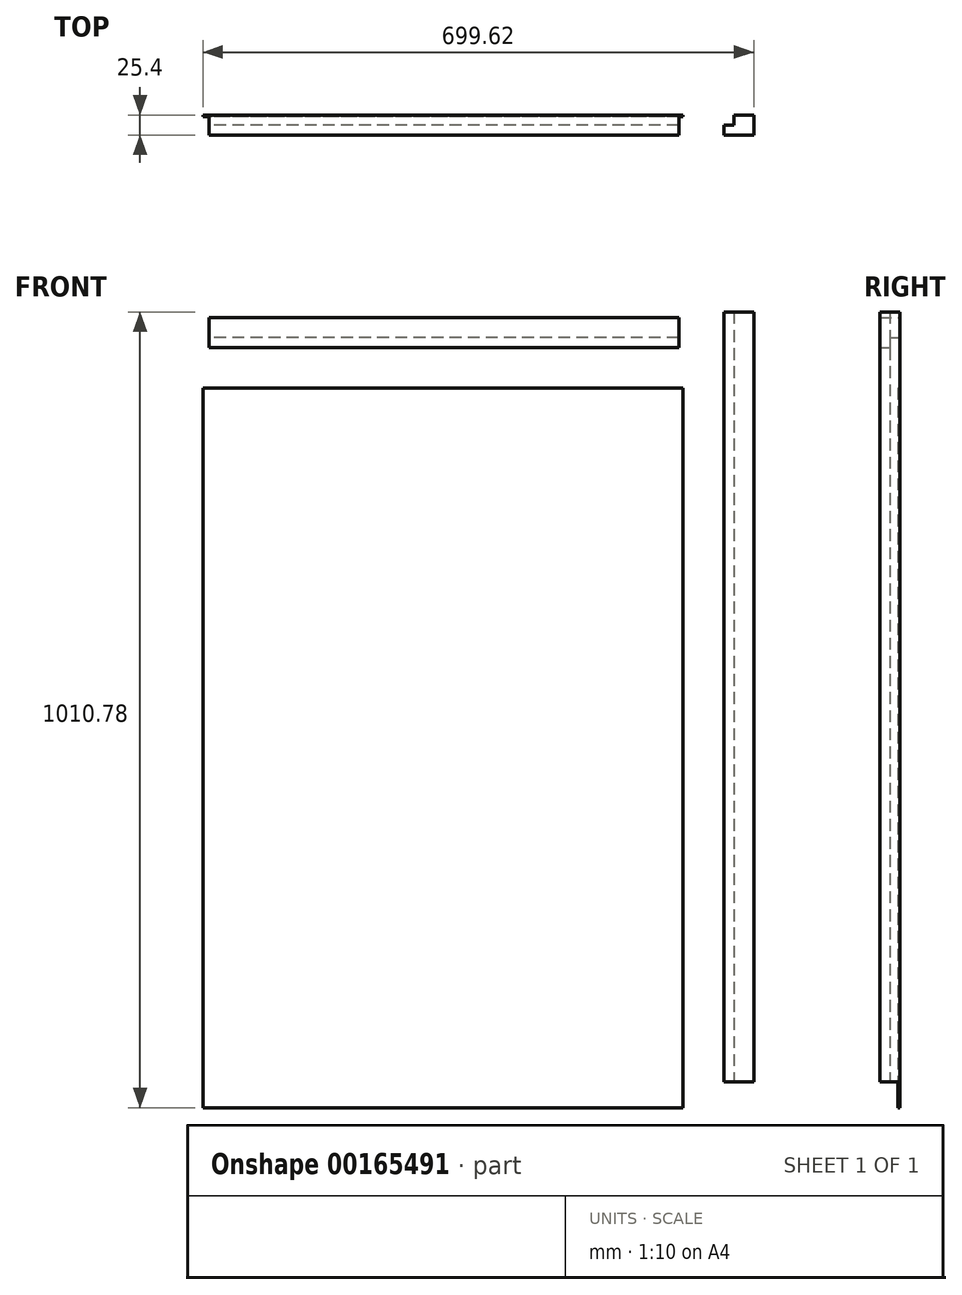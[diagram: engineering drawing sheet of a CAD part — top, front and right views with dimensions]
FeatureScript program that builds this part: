
annotation { "Feature Type Name" : "Feature", "Feature Type Description" : "" }
export const myFeature = defineFeature(function(context is Context, id is Id, definition is map)
    precondition{}
    {
        {
            var Q0;
            Q0=qCreatedBy(makeId("Front.planeOp"),FACE);
            var sketch = newSketch(context, id + "F0", { "sketchPlane" : qUnion([Q0])});
            skLineSegment(sketch, "E0.bottom", {"start": v(304.8, 457.2) * mm, "end": v(-304.8, 457.2) * mm});
            skLineSegment(sketch, "E0.top", {"start": v(304.8, -457.2) * mm, "end": v(-304.8, -457.2) * mm});
            skLineSegment(sketch, "E0.left", {"start": v(304.8, 457.2) * mm, "end": v(304.8, -457.2) * mm});
            skLineSegment(sketch, "E0.right", {"start": v(-304.8, 457.2) * mm, "end": v(-304.8, -457.2) * mm});
            skPoint(sketch, "E0.middle", {"position": v(0, 0) * mm});
            skSolve(sketch);
        }
        {
            var Q0;
            Q0 = qSketchRegion(id + "F0", true);
            extrude(context, id + "F1", {"entities" : qUnion([Q0]), "depth" : 2.38 * mm});
        }
        {
            var Q0;
            Q0=qCreatedBy(makeId("Front.planeOp"),FACE);
            var sketch = newSketch(context, id + "F2", { "sketchPlane" : qUnion([Q0])});
            skLineSegment(sketch, "E1.bottom", {"start": v(-297.3, 546.37) * mm, "end": v(299.6, 546.37) * mm});
            skLineSegment(sketch, "E1.top", {"start": v(-297.3, 508.27) * mm, "end": v(299.6, 508.27) * mm});
            skLineSegment(sketch, "E1.left", {"start": v(-297.3, 546.37) * mm, "end": v(-297.3, 508.27) * mm});
            skLineSegment(sketch, "E1.right", {"start": v(299.6, 546.37) * mm, "end": v(299.6, 508.27) * mm});
            skSolve(sketch);
        }
        {
            var Q0;
            Q0=qCreatedBy(makeId("Front.planeOp"),FACE);
            var sketch = newSketch(context, id + "F3", { "sketchPlane" : qUnion([Q0])});
            skLineSegment(sketch, "E2.bottom", {"start": v(356.72, 553.58) * mm, "end": v(394.82, 553.58) * mm});
            skLineSegment(sketch, "E2.top", {"start": v(356.72, -424.32) * mm, "end": v(394.82, -424.32) * mm});
            skLineSegment(sketch, "E2.left", {"start": v(356.72, 553.58) * mm, "end": v(356.72, -424.32) * mm});
            skLineSegment(sketch, "E2.right", {"start": v(394.82, 553.58) * mm, "end": v(394.82, -424.32) * mm});
            skSolve(sketch);
        }
        {
            var Q0;
            Q0=makeQuery(id+"F3.imprint","IMPRINT",FACE,{"disambiguationData":[TD([[makeQuery(id+"F3.imprint","IMPRINT",EDGE,{"derivedFrom":sQuery(id+"F3.wireOp",EDGE,"E2.bottom")}),-1.0]])]});
            extrude(context, id + "F4", {"entities" : qUnion([Q0]), "depth" : 25.4 * mm});
        }
        {
            var Q0;
            Q0=makeQuery(id+"F2.imprint","IMPRINT",FACE,{"disambiguationData":[TD([[makeQuery(id+"F2.imprint","IMPRINT",EDGE,{"derivedFrom":sQuery(id+"F2.wireOp",EDGE,"E1.bottom")}),-1.0]])]});
            extrude(context, id + "F5", {"entities" : qUnion([Q0]), "depth" : 25.4 * mm});
        }
        {
            var Q0;
            Q0=makeQuery(id+"F5.opExtrude","SWEPT_FACE",FACE,{"disambiguationData":[OSD([sQuery(id+"F2.wireOp",EDGE,"E1.left")])]});
            var sketch = newSketch(context, id + "F6", { "sketchPlane" : qUnion([Q0])});
            skLineSegment(sketch, "E3.bottom", {"start": v(0, 508.27) * mm, "end": v(12.7, 508.27) * mm});
            skLineSegment(sketch, "E3.top", {"start": v(0, 520.97) * mm, "end": v(12.7, 520.97) * mm});
            skLineSegment(sketch, "E3.left", {"start": v(0, 508.27) * mm, "end": v(0, 520.97) * mm});
            skLineSegment(sketch, "E3.right", {"start": v(12.7, 508.27) * mm, "end": v(12.7, 520.97) * mm});
            skSolve(sketch);
        }
        {
            var Q0;
            Q0=makeQuery(id+"F6.imprint","IMPRINT",FACE,{"disambiguationData":[TD([[makeQuery(id+"F6.imprint","IMPRINT",EDGE,{"derivedFrom":sQuery(id+"F6.wireOp",EDGE,"E3.bottom")}),-1.0]])]});
            extrude(context, id + "F7", {"entities" : qUnion([Q0]), "operationType" : NewBodyOperationType.REMOVE, "oppositeDirection" : true, "depth" : 609.6 * mm});
        }
        {
            var Q0;
            Q0=makeQuery(id+"F4.opExtrude","SWEPT_FACE",FACE,{"disambiguationData":[OSD([sQuery(id+"F3.wireOp",EDGE,"E2.top")])]});
            var sketch = newSketch(context, id + "F8", { "sketchPlane" : qUnion([Q0])});
            skLineSegment(sketch, "E4.bottom", {"start": v(356.72, 0) * mm, "end": v(369.42, 0) * mm});
            skLineSegment(sketch, "E4.top", {"start": v(356.72, 12.7) * mm, "end": v(369.42, 12.7) * mm});
            skLineSegment(sketch, "E4.left", {"start": v(356.72, 0) * mm, "end": v(356.72, 12.7) * mm});
            skLineSegment(sketch, "E4.right", {"start": v(369.42, 0) * mm, "end": v(369.42, 12.7) * mm});
            skSolve(sketch);
        }
        {
            var Q0;
            Q0=makeQuery(id+"F8.imprint","IMPRINT",FACE,{"disambiguationData":[TD([[makeQuery(id+"F8.imprint","IMPRINT",EDGE,{"derivedFrom":sQuery(id+"F8.wireOp",EDGE,"E4.bottom")}),1.0]])]});
            extrude(context, id + "F9", {"entities" : qUnion([Q0]), "operationType" : NewBodyOperationType.REMOVE, "endBound" : BoundingType.THROUGH_ALL, "oppositeDirection" : true, "depth" : 25.4 * mm});
        }
    });
